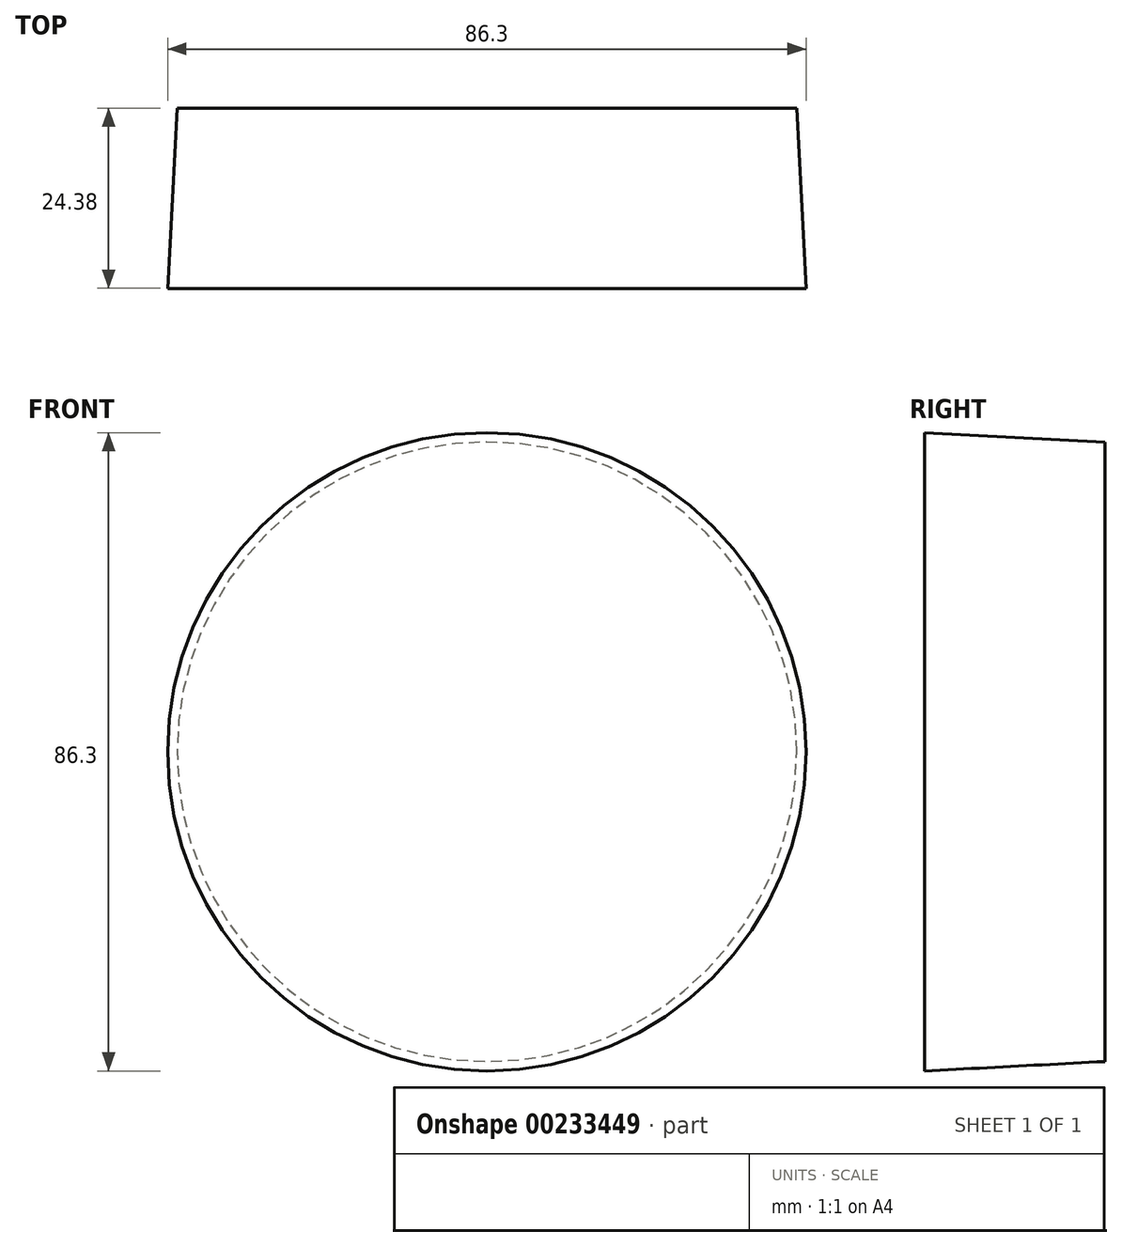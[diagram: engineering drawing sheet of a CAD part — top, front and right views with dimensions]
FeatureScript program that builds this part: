
annotation { "Feature Type Name" : "Feature", "Feature Type Description" : "" }
export const myFeature = defineFeature(function(context is Context, id is Id, definition is map)
    precondition{}
    {
        {
            var Q0;
            Q0=qCreatedBy(makeId("Front.planeOp"),FACE);
            var sketch = newSketch(context, id + "F0", { "sketchPlane" : qUnion([Q0])});
            skCircle(sketch, "E0", {"center": v(0, 0) * mm, "radius": 41.88 * mm});
            skSolve(sketch);
        }
        {
            var Q0;
            Q0=makeQuery(id+"F0.imprint","IMPRINT",FACE,{"disambiguationData":[TD([[makeQuery(id+"F0.imprint","IMPRINT",EDGE,{"derivedFrom":sQuery(id+"F0.wireOp",EDGE,"E0")}),1.0]])]});
            extrude(context, id + "F1", {"entities" : qUnion([Q0]), "depth" : 24.38 * mm, "hasDraft" : true, "draftAngle" : 3 * degree});
        }
    });
